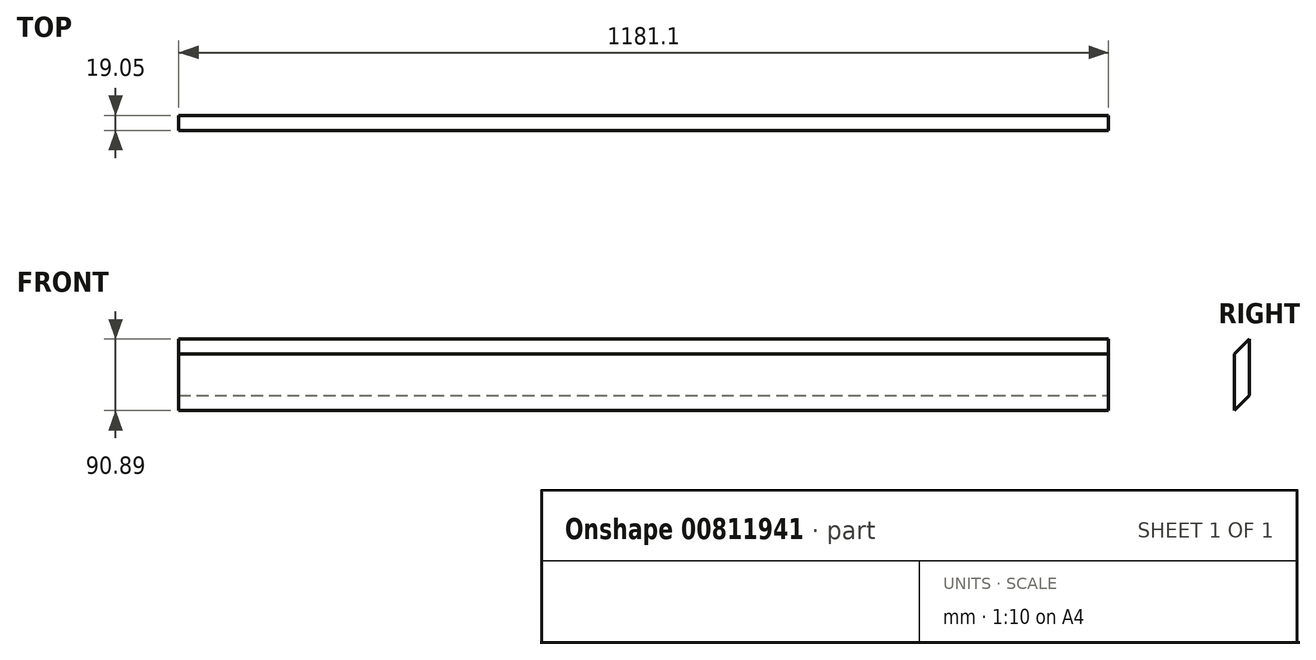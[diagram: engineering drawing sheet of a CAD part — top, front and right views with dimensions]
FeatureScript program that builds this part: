
annotation { "Feature Type Name" : "Feature", "Feature Type Description" : "" }
export const myFeature = defineFeature(function(context is Context, id is Id, definition is map)
    precondition{}
    {
        {
            var Q0;
            Q0=qCreatedBy(makeId("Front.planeOp"),FACE);
            var sketch = newSketch(context, id + "F0", { "sketchPlane" : qUnion([Q0])});
            skLineSegment(sketch, "E0.bottom", {"start": v(590.55, -35.92) * mm, "end": v(-590.55, -35.92) * mm});
            skLineSegment(sketch, "E0.top", {"start": v(590.55, 35.92) * mm, "end": v(-590.55, 35.92) * mm});
            skLineSegment(sketch, "E0.left", {"start": v(590.55, -35.92) * mm, "end": v(590.55, 35.92) * mm});
            skLineSegment(sketch, "E0.right", {"start": v(-590.55, -35.92) * mm, "end": v(-590.55, 35.92) * mm});
            skPoint(sketch, "E0.middle", {"position": v(0, 0) * mm});
            skSolve(sketch);
        }
        {
            var Q0;
            Q0 = qSketchRegion(id + "F0", true);
            extrude(context, id + "F1", {"entities" : qUnion([Q0]), "depth" : 19.05 * mm, "offsetDistance" : 25.4 * mm});
        }
        {
            var Q0;
            Q0=makeQuery(id+"F1.opExtrude","SWEPT_FACE",FACE,{"disambiguationData":[OSD([sQuery(id+"F0.wireOp",EDGE,"E0.left")])]});
            var sketch = newSketch(context, id + "F2", { "sketchPlane" : qUnion([Q0])});
            skLineSegment(sketch, "E1.0", {"start": v(-19.05, -35.92) * mm, "end": v(-19.05, 35.92) * mm, "construction": true});
            skPoint(sketch, "E2.0", {"position": v(-9.53, 35.92) * mm});
            skLineSegment(sketch, "E3.0", {"start": v(-19.05, 35.92) * mm, "end": v(0, 35.92) * mm, "construction": true});
            skLineSegment(sketch, "E4.0", {"start": v(0, -35.92) * mm, "end": v(0, 35.92) * mm, "construction": true});
            skPoint(sketch, "E5.0", {"position": v(-9.53, -35.92) * mm});
            skLineSegment(sketch, "E6.0", {"start": v(-19.05, -35.92) * mm, "end": v(0, -35.92) * mm, "construction": true});
            skLineSegment(sketch, "E7", {"start": v(-19.05, -35.92) * mm, "end": v(0, -16.87) * mm});
            skLineSegment(sketch, "E8", {"start": v(-19.05, -35.92) * mm, "end": v(0, -35.92) * mm});
            skLineSegment(sketch, "E9", {"start": v(0, -35.92) * mm, "end": v(0, -16.87) * mm});
            skSolve(sketch);
        }
        {
            var Q0;
            Q0 = qSketchRegion(id + "F2", true);
            extrude(context, id + "F3", {"entities" : qUnion([Q0]), "operationType" : NewBodyOperationType.REMOVE, "endBound" : BoundingType.THROUGH_ALL, "oppositeDirection" : true, "depth" : 25.4 * mm, "offsetDistance" : 25.4 * mm});
        }
        {
            var Q0;
            Q0=makeQuery(id+"F1.opExtrude","SWEPT_FACE",FACE,{"disambiguationData":[OSD([sQuery(id+"F0.wireOp",EDGE,"E0.left")])]});
            var sketch = newSketch(context, id + "F4", { "sketchPlane" : qUnion([Q0])});
            skLineSegment(sketch, "E10.0", {"start": v(-19.05, 35.92) * mm, "end": v(0, 35.92) * mm, "construction": true});
            skLineSegment(sketch, "E11.0", {"start": v(-19.05, -35.92) * mm, "end": v(-19.05, 35.92) * mm, "construction": true});
            skLineSegment(sketch, "E12.0", {"start": v(0, -16.87) * mm, "end": v(0, 35.92) * mm, "construction": true});
            skLineSegment(sketch, "E13", {"start": v(-19.05, 35.92) * mm, "end": v(0, 54.97) * mm});
            skLineSegment(sketch, "E14", {"start": v(-19.05, 35.92) * mm, "end": v(0, 35.92) * mm});
            skLineSegment(sketch, "E15", {"start": v(0, 54.97) * mm, "end": v(0, 35.92) * mm});
            skSolve(sketch);
        }
        {
            var Q0;
            Q0=makeQuery(id+"F4.imprint","IMPRINT",FACE,{"disambiguationData":[TD([[makeQuery(id+"F4.imprint","IMPRINT",EDGE,{"derivedFrom":sQuery(id+"F4.wireOp",EDGE,"E13")}),-1.0]])]});
            extrude(context, id + "F5", {"entities" : qUnion([Q0]), "operationType" : NewBodyOperationType.ADD, "oppositeDirection" : true, "depth" : 1181.1 * mm, "offsetDistance" : 25.4 * mm});
        }
    });
